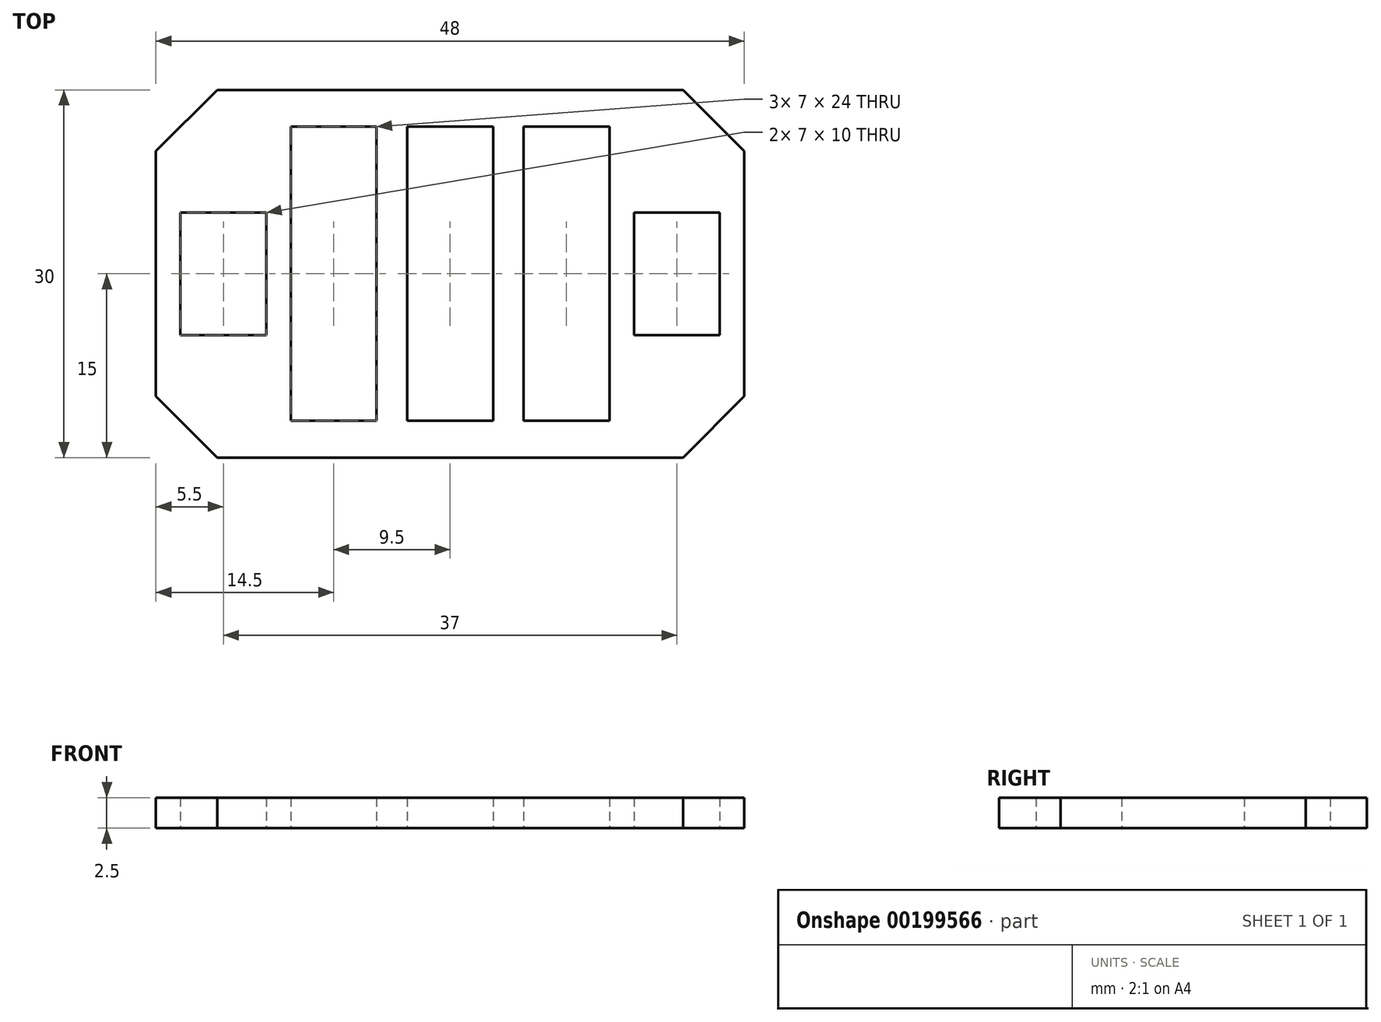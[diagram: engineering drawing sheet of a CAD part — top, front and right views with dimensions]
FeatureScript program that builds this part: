
annotation { "Feature Type Name" : "Feature", "Feature Type Description" : "" }
export const myFeature = defineFeature(function(context is Context, id is Id, definition is map)
    precondition{}
    {
        {
            var Q0;
            Q0=qCreatedBy(makeId("Top.planeOp"),FACE);
            var sketch = newSketch(context, id + "F0", { "sketchPlane" : qUnion([Q0])});
            skLineSegment(sketch, "E0.bottom", {"start": v(24, -15) * mm, "end": v(-24, -15) * mm});
            skLineSegment(sketch, "E0.top", {"start": v(24, 15) * mm, "end": v(-24, 15) * mm});
            skLineSegment(sketch, "E0.left", {"start": v(24, -15) * mm, "end": v(24, 15) * mm});
            skLineSegment(sketch, "E0.right", {"start": v(-24, -15) * mm, "end": v(-24, 15) * mm});
            skPoint(sketch, "E0.middle", {"position": v(0, 0) * mm});
            skLineSegment(sketch, "E1.bottom", {"start": v(3.5, -12) * mm, "end": v(-3.5, -12) * mm});
            skLineSegment(sketch, "E1.top", {"start": v(3.5, 12) * mm, "end": v(-3.5, 12) * mm});
            skLineSegment(sketch, "E1.left", {"start": v(3.5, -12) * mm, "end": v(3.5, 12) * mm});
            skLineSegment(sketch, "E1.right", {"start": v(-3.5, -12) * mm, "end": v(-3.5, 12) * mm});
            skLineSegment(sketch, "E2", {"start": v(-6, 12) * mm, "end": v(-6, -12) * mm});
            skLineSegment(sketch, "E3", {"start": v(6, 12) * mm, "end": v(6, -12) * mm});
            skLineSegment(sketch, "E4.bottom", {"start": v(-6, 12) * mm, "end": v(-13, 12) * mm});
            skLineSegment(sketch, "E4.top", {"start": v(-6, -12) * mm, "end": v(-13, -12) * mm});
            skLineSegment(sketch, "E4.right", {"start": v(-13, 12) * mm, "end": v(-13, -12) * mm});
            skLineSegment(sketch, "E5.bottom", {"start": v(6, 12) * mm, "end": v(13, 12) * mm});
            skLineSegment(sketch, "E5.top", {"start": v(6, -12) * mm, "end": v(13, -12) * mm});
            skLineSegment(sketch, "E5.right", {"start": v(13, 12) * mm, "end": v(13, -12) * mm});
            skLineSegment(sketch, "E6", {"start": v(-15, 5) * mm, "end": v(-15, -5) * mm});
            skLineSegment(sketch, "E7", {"start": v(15, 5) * mm, "end": v(15, -5) * mm});
            skLineSegment(sketch, "E8.bottom", {"start": v(22, -5) * mm, "end": v(15, -5) * mm});
            skLineSegment(sketch, "E8.top", {"start": v(22, 5) * mm, "end": v(15, 5) * mm});
            skLineSegment(sketch, "E8.left", {"start": v(22, -5) * mm, "end": v(22, 5) * mm});
            skLineSegment(sketch, "E8.right", {"start": v(-22, -5) * mm, "end": v(-22, 5) * mm});
            skLineSegment(sketch, "E9.trimOffspring", {"start": v(13, 12) * mm, "end": v(6, 12) * mm});
            skLineSegment(sketch, "E10.trimOffspring", {"start": v(-15, 5) * mm, "end": v(-22, 5) * mm});
            skLineSegment(sketch, "E11.trimOffspring", {"start": v(-15, -5) * mm, "end": v(-22, -5) * mm});
            skLineSegment(sketch, "E12.trimOffspring", {"start": v(22, 5) * mm, "end": v(22, -5) * mm});
            skSolve(sketch);
        }
        {
            var Q0;
            Q0=makeQuery(id+"F0.imprint","IMPRINT",FACE,{"disambiguationData":[TD([[makeQuery(id+"F0.imprint","IMPRINT",EDGE,{"derivedFrom":sQuery(id+"F0.wireOp",EDGE,"E5.top")}),1.0]])]});
            var Q1;
            Q1=makeQuery(id+"F0.imprint","IMPRINT",FACE,{"disambiguationData":[TD([[makeQuery(id+"F0.imprint","IMPRINT",EDGE,{"derivedFrom":sQuery(id+"F0.wireOp",EDGE,"E0.bottom")}),-1.0]])]});
            var Q2;
            Q2=makeQuery(id+"F0.imprint","IMPRINT",FACE,{"disambiguationData":[TD([[makeQuery(id+"F0.imprint","IMPRINT",EDGE,{"derivedFrom":sQuery(id+"F0.wireOp",EDGE,"E6")}),-1.0]])]});
            var Q3;
            Q3=makeQuery(id+"F0.imprint","IMPRINT",FACE,{"disambiguationData":[TD([[makeQuery(id+"F0.imprint","IMPRINT",EDGE,{"derivedFrom":sQuery(id+"F0.wireOp",EDGE,"E4.top")}),-1.0]])]});
            var Q4;
            Q4=makeQuery(id+"F0.imprint","IMPRINT",FACE,{"disambiguationData":[TD([[makeQuery(id+"F0.imprint","IMPRINT",EDGE,{"derivedFrom":sQuery(id+"F0.wireOp",EDGE,"E1.bottom")}),-1.0]])]});
            var Q5;
            Q5=makeQuery(id+"F0.imprint","IMPRINT",FACE,{"disambiguationData":[TD([[makeQuery(id+"F0.imprint","IMPRINT",EDGE,{"derivedFrom":sQuery(id+"F0.wireOp",EDGE,"E7")}),1.0]])]});
            extrude(context, id + "F1", {"entities" : qUnion([Q0, Q1, Q2, Q3, Q4, Q5]), "depth" : 2.5 * mm});
        }
        {
            var Q0;
            Q0=makeQuery(id+"F0.imprint","IMPRINT",FACE,{"disambiguationData":[TD([[makeQuery(id+"F0.imprint","IMPRINT",EDGE,{"derivedFrom":sQuery(id+"F0.wireOp",EDGE,"E6")}),-1.0]])]});
            var Q1;
            Q1=makeQuery(id+"F0.imprint","IMPRINT",FACE,{"disambiguationData":[TD([[makeQuery(id+"F0.imprint","IMPRINT",EDGE,{"derivedFrom":sQuery(id+"F0.wireOp",EDGE,"E7")}),1.0]])]});
            var Q2;
            Q2=makeQuery(id+"F0.imprint","IMPRINT",FACE,{"disambiguationData":[TD([[makeQuery(id+"F0.imprint","IMPRINT",EDGE,{"derivedFrom":sQuery(id+"F0.wireOp",EDGE,"E4.top")}),-1.0]])]});
            var Q3;
            Q3=makeQuery(id+"F0.imprint","IMPRINT",FACE,{"disambiguationData":[TD([[makeQuery(id+"F0.imprint","IMPRINT",EDGE,{"derivedFrom":sQuery(id+"F0.wireOp",EDGE,"E1.bottom")}),-1.0]])]});
            var Q4;
            Q4=makeQuery(id+"F0.imprint","IMPRINT",FACE,{"disambiguationData":[TD([[makeQuery(id+"F0.imprint","IMPRINT",EDGE,{"derivedFrom":sQuery(id+"F0.wireOp",EDGE,"E5.top")}),1.0]])]});
            extrude(context, id + "F2", {"entities" : qUnion([Q0, Q1, Q2, Q3, Q4]), "operationType" : NewBodyOperationType.REMOVE, "depth" : 2.5 * mm});
        }
        {
            var Q0;
            Q0=makeQuery(id+"F1.opExtrude","SWEPT_EDGE",EDGE,{"disambiguationData":[OSD([sQuery(id+"F0.wireOp",EDGE,"E0.bottom"),sQuery(id+"F0.wireOp",EDGE,"E0.left")])]});
            var Q1;
            Q1=makeQuery(id+"F1.opExtrude","SWEPT_EDGE",EDGE,{"disambiguationData":[OSD([sQuery(id+"F0.wireOp",EDGE,"E0.top"),sQuery(id+"F0.wireOp",EDGE,"E0.left")])]});
            var Q2;
            Q2=makeQuery(id+"F1.opExtrude","SWEPT_EDGE",EDGE,{"disambiguationData":[OSD([sQuery(id+"F0.wireOp",EDGE,"E0.top"),sQuery(id+"F0.wireOp",EDGE,"E0.right")])]});
            var Q3;
            Q3=makeQuery(id+"F1.opExtrude","SWEPT_EDGE",EDGE,{"disambiguationData":[OSD([sQuery(id+"F0.wireOp",EDGE,"E0.bottom"),sQuery(id+"F0.wireOp",EDGE,"E0.right")])]});
            chamfer(context, id + "F3", {"entities" : qUnion([Q0, Q1, Q2, Q3]), "chamferType" : ChamferType.OFFSET_ANGLE, "width" : 5 * mm, "oppositeDirection" : false, "angle" : 45 * degree, "tangentPropagation" : true});
        }
    });
